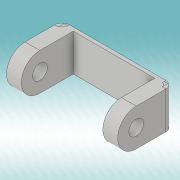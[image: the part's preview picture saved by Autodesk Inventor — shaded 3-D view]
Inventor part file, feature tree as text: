
AUTODESK INVENTOR PART (.ipt)
format: ipt  version: 2019 (Build 230136000, 136)  size: 223,744 bytes
history: native  units: in
note: dims shown in document units (in); Inventor stores cm internally (conversion verified against a paired STEP export)
features: sketch x10, extrude x6, sheet_metal_op x6, other x4
ambient origin geometry x8: Origin, YZ Plane, XZ Plane, XY Plane, X Axis, Y Axis, Z Axis, Center Point
bodies: Solid1 (feature_tree)
feature tree (26):
  extrude  "Extrusion1"  Depth=0.0787in TaperAngle=0.0deg
  sheet_metal_op  "Flange1"
  sheet_metal_op  "Flange2"
  extrude  "Extrusion3"  Depth=0.0787in
  extrude  "Extrusion4"  Depth=0.0787in
  extrude  "Extrusion5"  Depth=0.0787in
  extrude  "Extrusion6"  Depth=0.315in
  extrude  "Extrusion7"  Depth=0.0787in
  sketch  "Sketch1"  dims[d0=1.1811in d4=0.0787in d5=0.0in]
  sketch  "Sketch2"  dims[d6=0.7874in d7=0.0787in]
  other  "Plate1"
  sheet_metal_op  "Bend1"
  sheet_metal_op  "Corner1"
  sketch  "Sketch3"  dims[d8=0.0787in d9=0.0394in]
  other  "Plate2"
  sheet_metal_op  "Bend2"
  sheet_metal_op  "Corner2"
  sketch  "Sketch5"  dims[d10=0.1575in d11=0.0787in]
  sketch  "Sketch6"  dims[d12=1.1811in d13=90.0deg d14=0.0787in d15=0.315in]
  sketch  "Sketch8"  dims[d16=0.0787in d17=0.0787in]
  sketch  "Sketch9"  dims[d18=0.0787in]
  sketch  "Sketch11"  dims[d19=0.0394in]
  sketch  "Sketch12"  dims[d20=0.1575in]
  sketch  "Sketch13"  dims[d21=0.0787in d22=1.1811in d23=90.0deg d24=0.0787in d25=0.315in d26=0.0787in d27=0.0787in d38=0.3937in d39=0.3937in d40=0.3937in d41=0.0787in d42=0.0in d43=0.3937in d44=0.0787in d45=0.0in d46=0.315in d47=0.315in d54=0.315in d55=0.0in d56=0.2362in d57=0.0in d58=0.1181in d59=0.0in d60=0.1181in d61=0.0in d62=0.3937in d63=0.3937in d64=1.0236in d65=0.0039in d66=0.0in]
  other  "Cut1"
  other  "Cut2"
